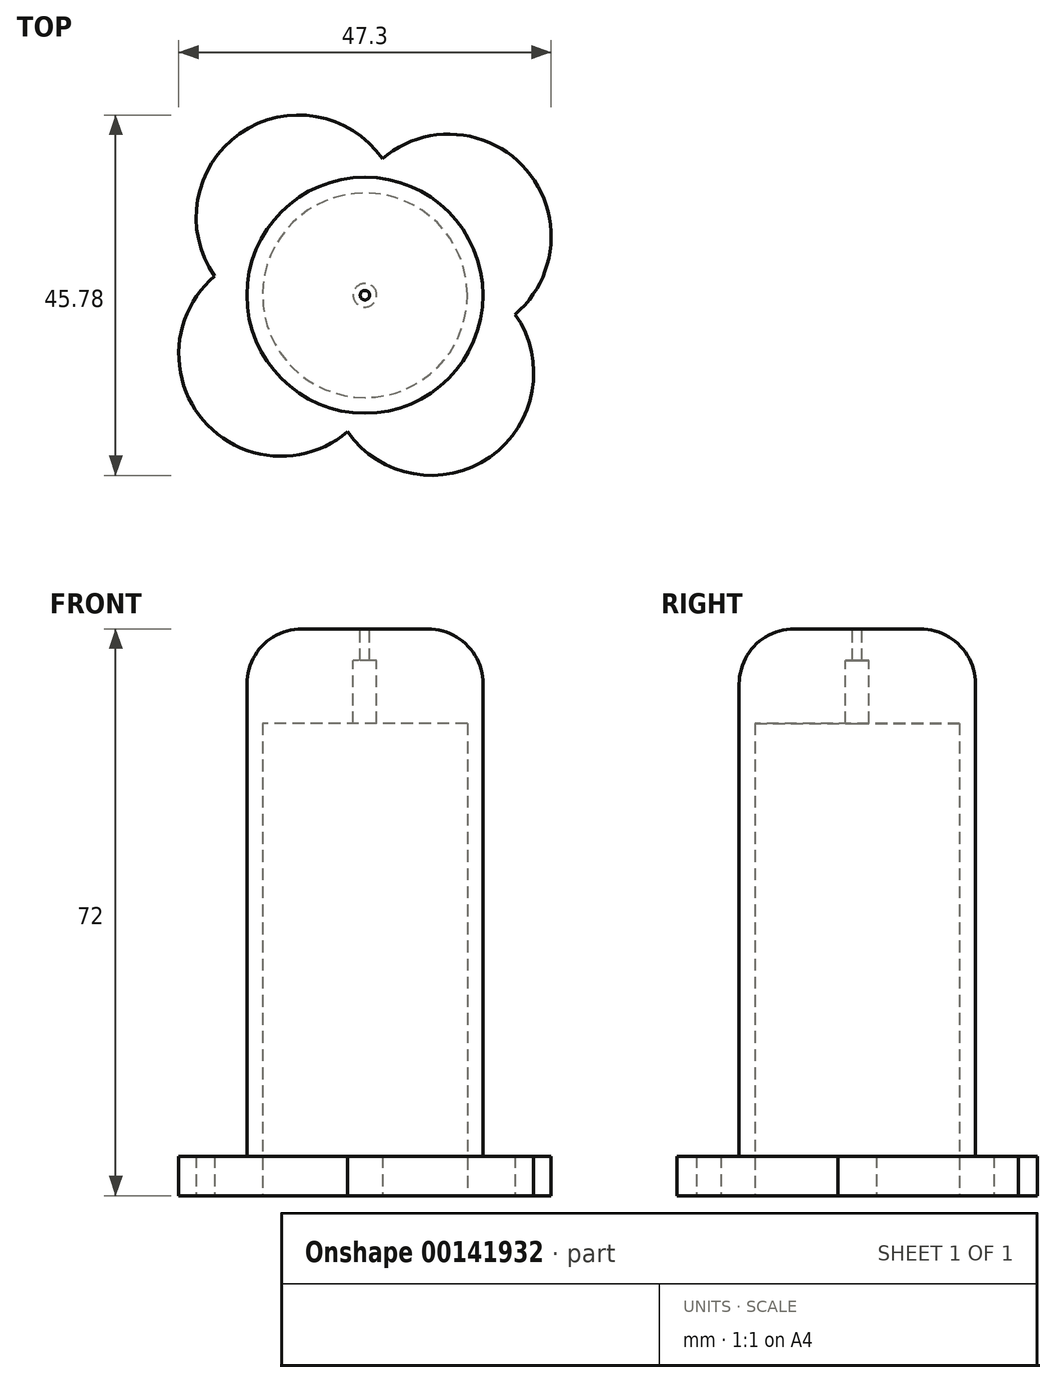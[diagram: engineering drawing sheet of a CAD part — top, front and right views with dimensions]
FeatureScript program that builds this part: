
annotation { "Feature Type Name" : "Feature", "Feature Type Description" : "" }
export const myFeature = defineFeature(function(context is Context, id is Id, definition is map)
    precondition{}
    {
        {
            var Q0;
            Q0=qCreatedBy(makeId("Top.planeOp"),FACE);
            var sketch = newSketch(context, id + "F0", { "sketchPlane" : qUnion([Q0])});
            skCircle(sketch, "E0", {"center": v(0, 0) * mm, "radius": 13 * mm});
            skCircle(sketch, "E1", {"center": v(10.65, 7.45) * mm, "radius": 13 * mm});
            skCircle(sketch, "E2", {"center": v(8.44, -9.89) * mm, "radius": 13 * mm});
            skCircle(sketch, "E3", {"center": v(-10.65, -7.45) * mm, "radius": 13 * mm});
            skCircle(sketch, "E4", {"center": v(-8.44, 9.89) * mm, "radius": 13 * mm});
            skCircle(sketch, "E5", {"center": v(0, 0) * mm, "radius": 15 * mm});
            skSolve(sketch);
        }
        {
            var Q0;
            {var subQ0=sQuery(id+"F0.wireOp",EDGE,"E4");var subQ1=sQuery(id+"F0.wireOp",EDGE,"E0");var subQ2=makeQuery(id+"F0.imprint","INTERSECT",VERTEX,{"disambiguationData":[OD(0.0)],"derivedFrom":[subQ1,subQ0]});Q0=makeQuery(id+"F0.imprint","IMPRINT",FACE,{"disambiguationData":[TD([[makeQuery(id+"F0.imprint","IMPRINT",EDGE,{"disambiguationData":[TD([[subQ2,1.0]])],"derivedFrom":subQ1}),-1.0]])]});}
            var Q1;
            {var subQ0=sQuery(id+"F0.wireOp",EDGE,"E2");var subQ1=sQuery(id+"F0.wireOp",EDGE,"E0");var subQ2=makeQuery(id+"F0.imprint","INTERSECT",VERTEX,{"disambiguationData":[OD(0.0)],"derivedFrom":[subQ1,subQ0]});Q1=makeQuery(id+"F0.imprint","IMPRINT",FACE,{"disambiguationData":[TD([[makeQuery(id+"F0.imprint","IMPRINT",EDGE,{"disambiguationData":[TD([[subQ2,1.0]])],"derivedFrom":subQ1}),-1.0]])]});}
            var Q2;
            {var subQ0=sQuery(id+"F0.wireOp",EDGE,"E3");var subQ1=sQuery(id+"F0.wireOp",EDGE,"E0");var subQ2=makeQuery(id+"F0.imprint","INTERSECT",VERTEX,{"disambiguationData":[OD(1.0)],"derivedFrom":[subQ1,subQ0]});Q2=makeQuery(id+"F0.imprint","IMPRINT",FACE,{"disambiguationData":[TD([[makeQuery(id+"F0.imprint","IMPRINT",EDGE,{"disambiguationData":[TD([[subQ2,-1.0]])],"derivedFrom":subQ1}),-1.0]])]});}
            var Q3;
            {var subQ0=sQuery(id+"F0.wireOp",EDGE,"E2");var subQ1=sQuery(id+"F0.wireOp",EDGE,"E0");var subQ2=makeQuery(id+"F0.imprint","INTERSECT",VERTEX,{"disambiguationData":[OD(1.0)],"derivedFrom":[subQ1,subQ0]});Q3=makeQuery(id+"F0.imprint","IMPRINT",FACE,{"disambiguationData":[TD([[makeQuery(id+"F0.imprint","IMPRINT",EDGE,{"disambiguationData":[TD([[subQ2,-1.0]])],"derivedFrom":subQ1}),-1.0]])]});}
            var Q4;
            {var subQ0=sQuery(id+"F0.wireOp",EDGE,"E4");var subQ1=sQuery(id+"F0.wireOp",EDGE,"E0");var subQ2=makeQuery(id+"F0.imprint","INTERSECT",VERTEX,{"disambiguationData":[OD(1.0)],"derivedFrom":[subQ1,subQ0]});Q4=makeQuery(id+"F0.imprint","IMPRINT",FACE,{"disambiguationData":[TD([[makeQuery(id+"F0.imprint","IMPRINT",EDGE,{"disambiguationData":[TD([[subQ2,-1.0]])],"derivedFrom":subQ1}),-1.0]])]});}
            var Q5;
            {var subQ0=sQuery(id+"F0.wireOp",EDGE,"E3");var subQ1=sQuery(id+"F0.wireOp",EDGE,"E0");var subQ2=makeQuery(id+"F0.imprint","INTERSECT",VERTEX,{"disambiguationData":[OD(0.0)],"derivedFrom":[subQ1,subQ0]});Q5=makeQuery(id+"F0.imprint","IMPRINT",FACE,{"disambiguationData":[TD([[makeQuery(id+"F0.imprint","IMPRINT",EDGE,{"disambiguationData":[TD([[subQ2,-1.0]])],"derivedFrom":subQ1}),-1.0]])]});}
            var Q6;
            {var subQ0=sQuery(id+"F0.wireOp",EDGE,"E1");var subQ1=sQuery(id+"F0.wireOp",EDGE,"E0");var subQ2=makeQuery(id+"F0.imprint","INTERSECT",VERTEX,{"disambiguationData":[OD(0.0)],"derivedFrom":[subQ1,subQ0]});Q6=makeQuery(id+"F0.imprint","IMPRINT",FACE,{"disambiguationData":[TD([[makeQuery(id+"F0.imprint","IMPRINT",EDGE,{"disambiguationData":[TD([[subQ2,-1.0]])],"derivedFrom":subQ1}),-1.0]])]});}
            var Q7;
            {var subQ0=sQuery(id+"F0.wireOp",EDGE,"E4");var subQ1=sQuery(id+"F0.wireOp",EDGE,"E0");var subQ2=makeQuery(id+"F0.imprint","INTERSECT",VERTEX,{"disambiguationData":[OD(0.0)],"derivedFrom":[subQ1,subQ0]});Q7=makeQuery(id+"F0.imprint","IMPRINT",FACE,{"disambiguationData":[TD([[makeQuery(id+"F0.imprint","IMPRINT",EDGE,{"disambiguationData":[TD([[subQ2,-1.0]])],"derivedFrom":subQ1}),-1.0]])]});}
            extrude(context, id + "F1", {"entities" : qUnion([Q0, Q1, Q2, Q3, Q4, Q5, Q6, Q7]), "depth" : 60 * mm});
        }
        {
            var Q0;
            {var subQ0=sQuery(id+"F0.wireOp",EDGE,"E2");var subQ1=sQuery(id+"F0.wireOp",EDGE,"E1");var subQ2=makeQuery(id+"F0.imprint","INTERSECT",VERTEX,{"derivedFrom":[subQ1,subQ0]});Q0=makeQuery(id+"F0.imprint","IMPRINT",FACE,{"disambiguationData":[TD([[makeQuery(id+"F0.imprint","IMPRINT",EDGE,{"disambiguationData":[TD([[subQ2,1.0]])],"derivedFrom":subQ1}),-1.0]])]});}
            var Q1;
            {var subQ0=sQuery(id+"F0.wireOp",EDGE,"E4");var subQ1=sQuery(id+"F0.wireOp",EDGE,"E1");var subQ2=makeQuery(id+"F0.imprint","INTERSECT",VERTEX,{"derivedFrom":[subQ1,subQ0]});Q1=makeQuery(id+"F0.imprint","IMPRINT",FACE,{"disambiguationData":[TD([[makeQuery(id+"F0.imprint","IMPRINT",EDGE,{"disambiguationData":[TD([[subQ2,1.0]])],"derivedFrom":subQ1}),1.0]])]});}
            var Q2;
            {var subQ0=sQuery(id+"F0.wireOp",EDGE,"E2");var subQ1=sQuery(id+"F0.wireOp",EDGE,"E1");var subQ2=makeQuery(id+"F0.imprint","INTERSECT",VERTEX,{"derivedFrom":[subQ1,subQ0]});Q2=makeQuery(id+"F0.imprint","IMPRINT",FACE,{"disambiguationData":[TD([[makeQuery(id+"F0.imprint","IMPRINT",EDGE,{"disambiguationData":[TD([[subQ2,1.0]])],"derivedFrom":subQ1}),1.0]])]});}
            var Q3;
            {var subQ0=sQuery(id+"F0.wireOp",EDGE,"E3");var subQ1=sQuery(id+"F0.wireOp",EDGE,"E2");var subQ2=makeQuery(id+"F0.imprint","INTERSECT",VERTEX,{"derivedFrom":[subQ1,subQ0]});Q3=makeQuery(id+"F0.imprint","IMPRINT",FACE,{"disambiguationData":[TD([[makeQuery(id+"F0.imprint","IMPRINT",EDGE,{"disambiguationData":[TD([[subQ2,1.0]])],"derivedFrom":subQ1}),1.0]])]});}
            var Q4;
            {var subQ0=sQuery(id+"F0.wireOp",EDGE,"E3");var subQ1=sQuery(id+"F0.wireOp",EDGE,"E2");var subQ2=makeQuery(id+"F0.imprint","INTERSECT",VERTEX,{"derivedFrom":[subQ1,subQ0]});Q4=makeQuery(id+"F0.imprint","IMPRINT",FACE,{"disambiguationData":[TD([[makeQuery(id+"F0.imprint","IMPRINT",EDGE,{"disambiguationData":[TD([[subQ2,1.0]])],"derivedFrom":subQ1}),-1.0]])]});}
            var Q5;
            {var subQ0=sQuery(id+"F0.wireOp",EDGE,"E4");var subQ1=sQuery(id+"F0.wireOp",EDGE,"E3");var subQ2=makeQuery(id+"F0.imprint","INTERSECT",VERTEX,{"derivedFrom":[subQ1,subQ0]});Q5=makeQuery(id+"F0.imprint","IMPRINT",FACE,{"disambiguationData":[TD([[makeQuery(id+"F0.imprint","IMPRINT",EDGE,{"disambiguationData":[TD([[subQ2,1.0]])],"derivedFrom":subQ1}),1.0]])]});}
            var Q6;
            {var subQ0=sQuery(id+"F0.wireOp",EDGE,"E4");var subQ1=sQuery(id+"F0.wireOp",EDGE,"E1");var subQ2=makeQuery(id+"F0.imprint","INTERSECT",VERTEX,{"derivedFrom":[subQ1,subQ0]});Q6=makeQuery(id+"F0.imprint","IMPRINT",FACE,{"disambiguationData":[TD([[makeQuery(id+"F0.imprint","IMPRINT",EDGE,{"disambiguationData":[TD([[subQ2,-1.0]])],"derivedFrom":subQ1}),-1.0]])]});}
            var Q7;
            {var subQ0=sQuery(id+"F0.wireOp",EDGE,"E4");var subQ1=sQuery(id+"F0.wireOp",EDGE,"E1");var subQ2=makeQuery(id+"F0.imprint","INTERSECT",VERTEX,{"derivedFrom":[subQ1,subQ0]});Q7=makeQuery(id+"F0.imprint","IMPRINT",FACE,{"disambiguationData":[TD([[makeQuery(id+"F0.imprint","IMPRINT",EDGE,{"disambiguationData":[TD([[subQ2,-1.0]])],"derivedFrom":subQ1}),1.0]])]});}
            extrude(context, id + "F2", {"entities" : qUnion([Q0, Q1, Q2, Q3, Q4, Q5, Q6, Q7]), "operationType" : NewBodyOperationType.ADD, "depth" : 5 * mm});
        }
        {
            var Q0;
            Q0=makeQuery(id+"F1.opExtrude","CAP_FACE",FACE,{"disambiguationData":[OSD([sQuery(id+"F0.wireOp",EDGE,"E0"),sQuery(id+"F0.wireOp",EDGE,"E5")])],"isStart":false});
            var sketch = newSketch(context, id + "F3", { "sketchPlane" : qUnion([Q0])});
            skCircle(sketch, "E6", {"center": v(0, 0) * mm, "radius": 15 * mm});
            skSolve(sketch);
        }
        {
            var Q0;
            Q0 = qSketchRegion(id + "F3", true);
            extrude(context, id + "F4", {"entities" : qUnion([Q0]), "operationType" : NewBodyOperationType.ADD, "depth" : 8 * mm});
        }
        {
            var Q0;
            Q0=makeQuery(id+"F4.opExtrude","CAP_FACE",FACE,{"disambiguationData":[OSD([sQuery(id+"F3.wireOp",EDGE,"E6")])],"isStart":false});
            var sketch = newSketch(context, id + "F5", { "sketchPlane" : qUnion([Q0])});
            skCircle(sketch, "E7", {"center": v(0, 0) * mm, "radius": 1.5 * mm});
            skSolve(sketch);
        }
        {
            var Q0;
            Q0 = qSketchRegion(id + "F5", true);
            extrude(context, id + "F6", {"entities" : qUnion([Q0]), "operationType" : NewBodyOperationType.REMOVE, "endBound" : BoundingType.THROUGH_ALL, "oppositeDirection" : true, "depth" : 25 * mm});
        }
        {
            var Q0;
            Q0=makeQuery(id+"F4.opExtrude","CAP_FACE",FACE,{"disambiguationData":[OSD([sQuery(id+"F3.wireOp",EDGE,"E6")])],"isStart":false});
            var sketch = newSketch(context, id + "F7", { "sketchPlane" : qUnion([Q0])});
            skCircle(sketch, "E8", {"center": v(0, 0) * mm, "radius": 15 * mm});
            skSolve(sketch);
        }
        {
            var Q0;
            Q0 = qSketchRegion(id + "F7", true);
            extrude(context, id + "F8", {"entities" : qUnion([Q0]), "operationType" : NewBodyOperationType.ADD, "depth" : 4 * mm});
        }
        {
            var Q0;
            Q0=makeQuery(id+"F8.opExtrude","CAP_FACE",FACE,{"disambiguationData":[OSD([sQuery(id+"F7.wireOp",EDGE,"E8")])],"isStart":false});
            var sketch = newSketch(context, id + "F9", { "sketchPlane" : qUnion([Q0])});
            skCircle(sketch, "E9", {"center": v(0, 0) * mm, "radius": 0.6 * mm});
            skSolve(sketch);
        }
        {
            var Q0;
            Q0=makeQuery(id+"F8.opExtrude","CAP_EDGE",EDGE,{"disambiguationData":[OSD([sQuery(id+"F7.wireOp",EDGE,"E8")])],"isStart":false});
            fillet(context, id + "F10", {"entities" : qUnion([Q0]), "radius" : 7 * mm, "tangentPropagation" : true, "allowEdgeOverflow" : false});
        }
        {
            var Q0;
            Q0 = qSketchRegion(id + "F9", true);
            extrude(context, id + "F11", {"entities" : qUnion([Q0]), "operationType" : NewBodyOperationType.REMOVE, "endBound" : BoundingType.THROUGH_ALL, "oppositeDirection" : true, "depth" : 25 * mm});
        }
    });
